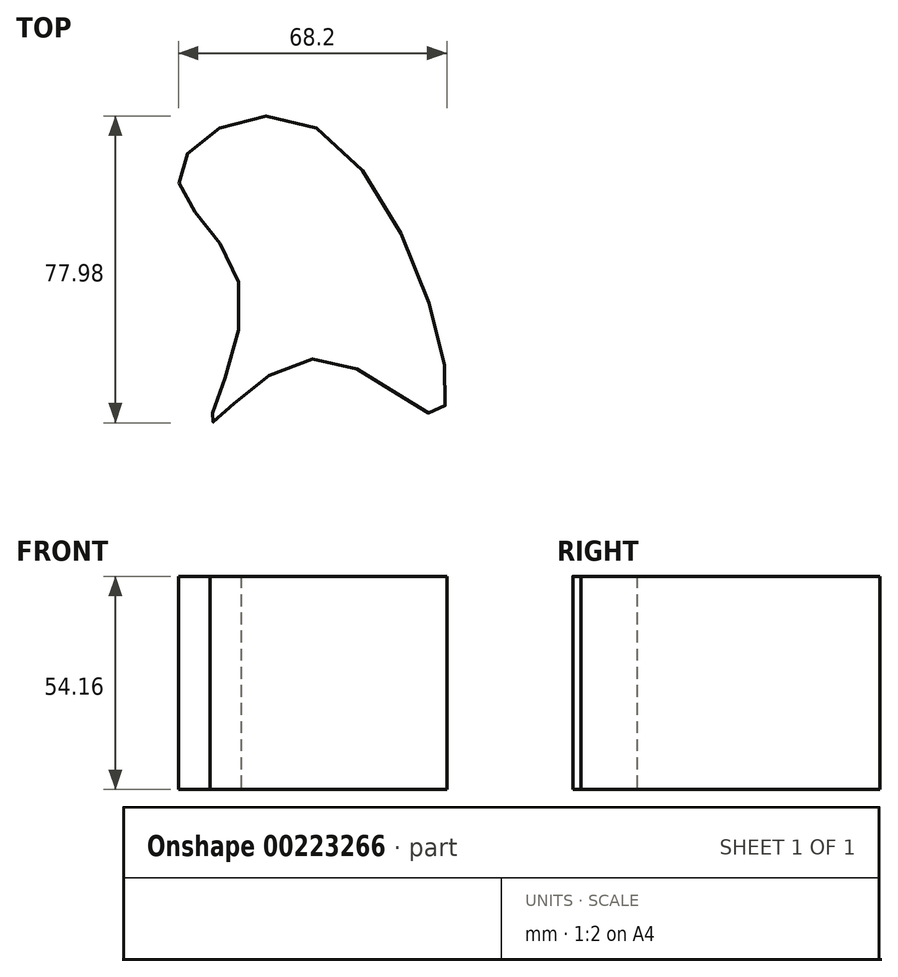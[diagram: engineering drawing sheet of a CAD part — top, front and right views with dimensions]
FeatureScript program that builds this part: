
annotation { "Feature Type Name" : "Feature", "Feature Type Description" : "" }
export const myFeature = defineFeature(function(context is Context, id is Id, definition is map)
    precondition{}
    {
        {
            var Q0;
            Q0=qCreatedBy(makeId("Top.planeOp"),FACE);
            var sketch = newSketch(context, id + "F0", { "sketchPlane" : qUnion([Q0])});
            skFitSpline(sketch, "E0", {"points": [v(0, 40.57) * mm, v(-35.01, 29.09) * mm, v(-19.45, 0) * mm, v(-26.86, -34.27) * mm, v(0, -17.97) * mm, v(31.68, -31.68) * mm, v(0, 40.57) * mm]});
            skSolve(sketch);
        }
        {
            var Q0;
            Q0=makeQuery(id+"F0.imprint","IMPRINT",FACE,{"disambiguationData":[TD([[makeQuery(id+"F0.imprint","IMPRINT",EDGE,{"derivedFrom":sQuery(id+"F0.wireOp",EDGE,"E0")}),1.0]])]});
            extrude(context, id + "F1", {"entities" : qUnion([Q0]), "depth" : 54.16 * mm});
        }
    });
